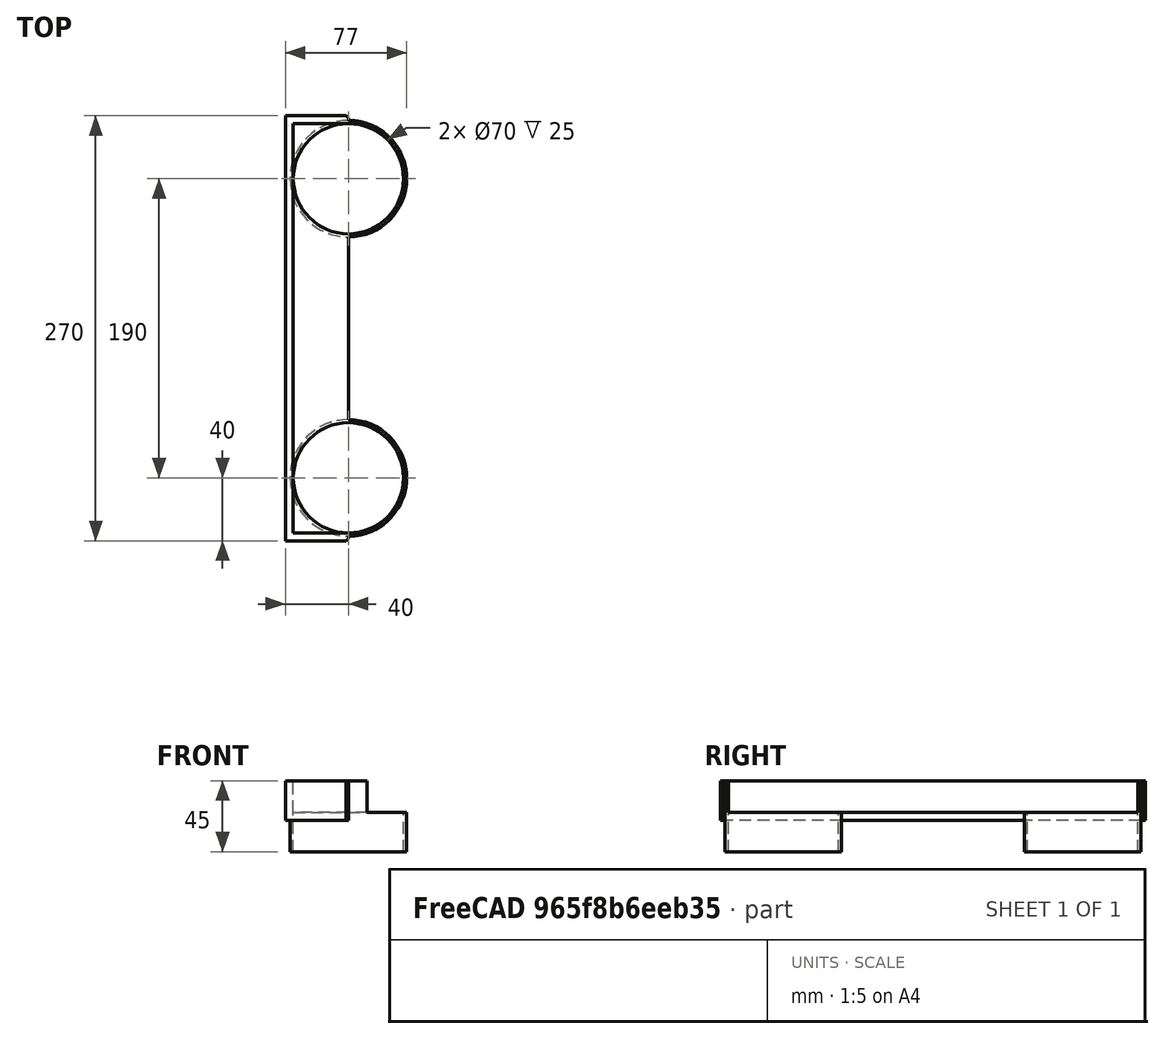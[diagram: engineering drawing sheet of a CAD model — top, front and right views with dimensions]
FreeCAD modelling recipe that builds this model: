
FCSTD DOCUMENT  (FreeCAD 0.18.3R)
Label: Hyllestotter
License: All rights reserved
LicenseURL: http://en.wikipedia.org/wiki/All_rights_reserved
objects: Part::Cylinder×4, Part::Cut×3, Part::Box×2, Part::MultiFuse×1, Part::Chamfer×1
note: 11 computed .brp shape members not serialized (recipe doc carries the construction recipe); baked Part::Feature solids carry a one-line shape summary decoded from their .brp

FEATURE [Part::Box] Box  label="Main"
  AttacherType = Attacher::AttachEngine3D
  Height = 25
  Length = 40
  Width = 270
FEATURE [Part::Box] Box001  label="Main cutout"
  AttacherType = Attacher::AttachEngine3D
  Height = 50
  Length = 102
  Placement = pos=(5,5,5) rot=(0,0,1;0rad)
  Width = 260
FEATURE [Part::Cylinder] Cylinder  label="Leg 1"
  Angle = 360
  AttacherType = Attacher::AttachEngine3D
  Height = 45
  Placement = pos=(40,40,-20) rot=(0,0,1;0rad)
  Radius = 37
FEATURE [Part::Cylinder] Cylinder001  label="Leg hole 1"
  Angle = 360
  AttacherType = Attacher::AttachEngine3D
  Height = 50
  Placement = pos=(40,40,-45) rot=(0,0,1;0rad)
  Radius = 35
FEATURE [Part::Cylinder] Cylinder002  label="Leg hole 2"
  Angle = 360
  AttacherType = Attacher::AttachEngine3D
  Height = 50
  Placement = pos=(40,230,-45) rot=(0,0,1;0rad)
  Radius = 35
FEATURE [Part::Cylinder] Cylinder003  label="Leg 2"
  Angle = 360
  AttacherType = Attacher::AttachEngine3D
  Height = 45
  Placement = pos=(40,230,-20) rot=(0,0,1;0rad)
  Radius = 37
FEATURE [Part::MultiFuse] Fusion  label="Main holder"
  Shapes = -> [Box,Cylinder,Cylinder003]
FEATURE [Part::Cut] Cut
  Base = -> Fusion
  Tool = -> Box001
FEATURE [Part::Cut] Cut001
  Base = -> Cut
  Tool = -> Cylinder001
FEATURE [Part::Cut] Cut002
  Base = -> Cut001
  Tool = -> Cylinder002
FEATURE [Part::Chamfer] Chamfer
  Base = -> Cut002
  Edges = 2 edges r=1.5: [Edge6,Edge21]
